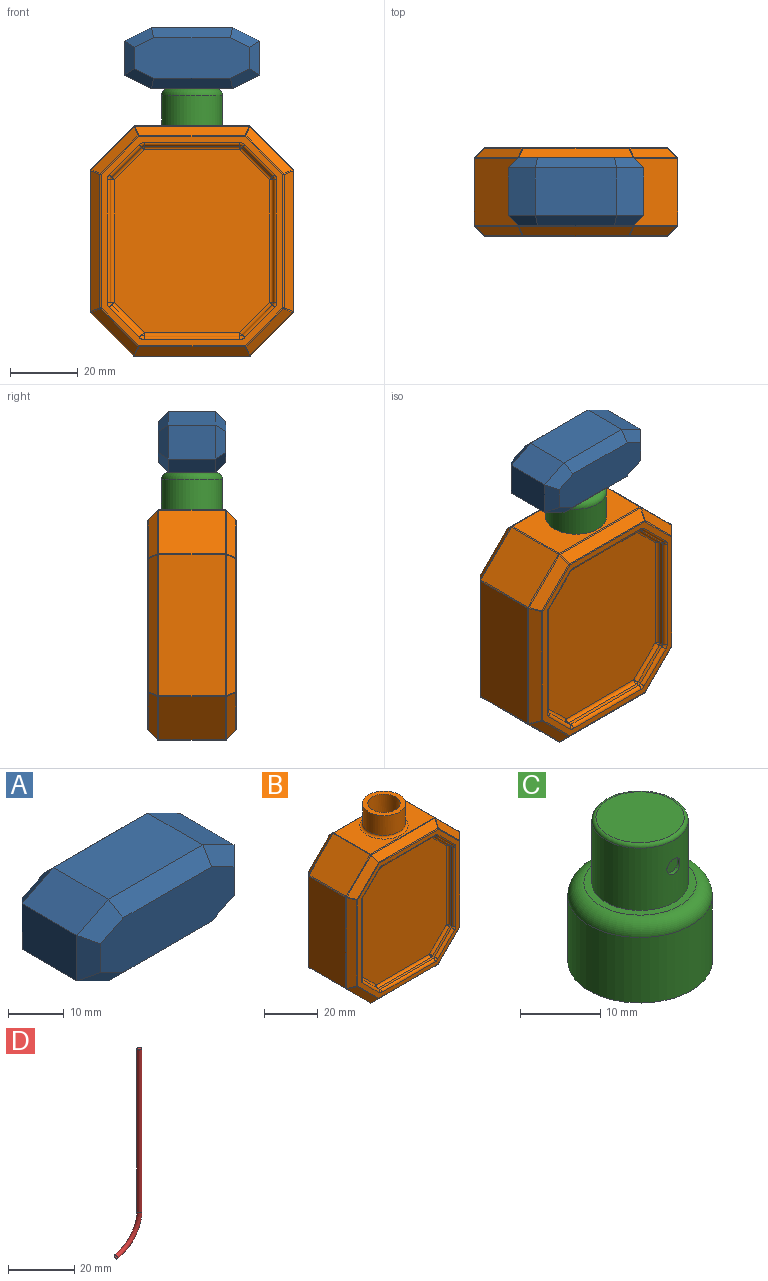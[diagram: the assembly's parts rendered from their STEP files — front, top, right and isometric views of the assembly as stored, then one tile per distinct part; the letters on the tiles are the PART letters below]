
ASSEMBLY  parts=4 mates=6
PART A: 29 faces, bbox 40x20x18 mm
  f0: plane 24x14mm, normal (0,0,1), area 336mm2, adj f1,f7,f16,f24
  f1: plane 14x8mm, normal (-0.45,0,0.89), area 125.2mm2, adj f0,f2,f14,f22
  f2: plane 14x10mm, normal (-1,0,0), area 140mm2, adj f1,f3,f12,f20
  f3: plane 14x8mm, normal (-0.45,0,-0.89), area 125.2mm2, adj f2,f4,f10,f18
  f4: plane 24x14mm, normal (0,0,-1), area 222.9mm2, adj f3,f5,f11,f19,f26
  f5: plane 14x8mm, normal (0.45,0,-0.89), area 125.2mm2, adj f4,f6,f13,f21
  f6: plane 14x10mm, normal (1,0,0), area 140mm2, adj f5,f7,f15,f23
  f7: plane 14x8mm, normal (0.45,0,0.89), area 125.2mm2, adj f0,f6,f17,f25
  f8: plane 34x12mm, normal (0,-1,0), area 375.4mm2, adj f18,f19,f20,f21,f22,f23,f24,f25
  f9: plane 34x12mm, normal (0,1,0), area 375.4mm2, adj f10,f11,f12,f13,f14,f15,f16,f17
  f10: plane 8.71x5.85mm, normal (-0.32,0.71,-0.63), area 32.5mm2, adj f3,f9,f11,f12
  f11: plane 24x3mm, normal (0,0.71,-0.71), area 98.8mm2, adj f4,f9,f10,f13
  f12: plane 10x3mm, normal (-0.71,0.71,0), area 34.6mm2, adj f2,f9,f10,f14
  f13: plane 8.71x5.85mm, normal (0.32,0.71,-0.63), area 32.5mm2, adj f5,f9,f11,f15
  f14: plane 8.71x5.85mm, normal (-0.32,0.71,0.63), area 32.5mm2, adj f1,f9,f12,f16
  f15: plane 10x3mm, normal (0.71,0.71,0), area 34.6mm2, adj f6,f9,f13,f17
  f16: plane 24x3mm, normal (0,0.71,0.71), area 98.8mm2, adj f0,f9,f14,f17
  f17: plane 8.71x5.85mm, normal (0.32,0.71,0.63), area 32.5mm2, adj f7,f9,f15,f16
  f18: plane 8.71x5.85mm, normal (-0.32,-0.71,-0.63), area 32.5mm2, adj f3,f8,f19,f20
  f19: plane 24x3mm, normal (0,-0.71,-0.71), area 98.8mm2, adj f4,f8,f18,f21
  f20: plane 10x3mm, normal (-0.71,-0.71,0), area 34.6mm2, adj f2,f8,f18,f22
  f21: plane 8.71x5.85mm, normal (0.32,-0.71,-0.63), area 32.5mm2, adj f5,f8,f19,f23
  f22: plane 8.71x5.85mm, normal (-0.32,-0.71,0.63), area 32.5mm2, adj f1,f8,f20,f24
  f23: plane 10x3mm, normal (0.71,-0.71,0), area 34.6mm2, adj f6,f8,f21,f25
  f24: plane 24x3mm, normal (0,-0.71,0.71), area 98.8mm2, adj f0,f8,f22,f25
  f25: plane 8.71x5.85mm, normal (0.32,-0.71,0.63), area 32.5mm2, adj f7,f8,f23,f24
  f26: cylinder r=6mm len=12mm, axis (0,0,-1), area 358.1mm2, adj f4,f28
  f27: plane 11x11mm, normal (0,0,-1), area 95mm2, adj f28
  f28: torus R=5.5mm, axis (0,0,-1), area 28.7mm2, adj f26,f27
PART B: 277 faces, bbox 60x26x78 mm
  f0: plane 19.59x12.71mm, normal (0.71,0,0.71), area 352mm2, adj f174,f175,f192,f193
  f1: plane 33.59x19.59mm, normal (0,0,1), area 403.3mm2, adj f185,f192,f199,f200,f214
  f2: plane 19.59x12.71mm, normal (-0.71,0,0.71), area 352mm2, adj f182,f183,f198,f199
  f3: plane 41.59x19.59mm, normal (-1,0,0), area 814.5mm2, adj f160,f161,f181,f182
  f4: plane 19.59x12.71mm, normal (-0.71,0,-0.71), area 352mm2, adj f141,f142,f159,f160
  f5: plane 33.59x19.59mm, normal (0,0,-1), area 657.8mm2, adj f129,f139,f140,f141
  f6: plane 19.59x12.71mm, normal (0.71,0,-0.71), area 352mm2, adj f138,f139,f154,f155
  f7: plane 41.59x19.59mm, normal (1,0,0), area 814.5mm2, adj f153,f154,f175,f176
  f8: plane 61.59x53.59mm, normal (0,-1,0), area 356.3mm2, adj f86,f90,f91,f95,f96,f100,f101,f105
  f9: plane 61.59x53.59mm, normal (0,1,0), area 356.3mm2, adj f46,f50,f51,f55,f56,f60,f61,f65
  f10: plane 13.83x13.83mm, normal (-0.5,0.71,-0.5), area 64.5mm2, adj f130,f131,f142,f143
  f11: plane 33.59x2.71mm, normal (0,0.71,-0.71), area 124.3mm2, adj f124,f128,f129,f130
  f12: plane 41.59x2.71mm, normal (-0.71,0.71,0), area 154.9mm2, adj f143,f144,f161,f162
  f13: plane 13.83x13.83mm, normal (0.5,0.71,-0.5), area 64.5mm2, adj f127,f128,f137,f138
  f14: plane 13.83x13.83mm, normal (-0.5,0.71,0.5), area 64.5mm2, adj f162,f163,f183,f184
  f15: plane 41.59x2.71mm, normal (0.71,0.71,0), area 154.9mm2, adj f136,f137,f152,f153
  f16: plane 33.59x2.71mm, normal (0,0.71,0.71), area 124.3mm2, adj f164,f173,f184,f185
  f17: plane 13.83x13.83mm, normal (0.5,0.71,0.5), area 64.5mm2, adj f151,f152,f173,f174
  f18: plane 13.83x13.83mm, normal (-0.5,-0.71,-0.5), area 64.5mm2, adj f158,f159,f179,f180
  f19: plane 33.59x2.71mm, normal (0,-0.71,-0.71), area 124.3mm2, adj f140,f156,f157,f158
  f20: plane 41.59x2.71mm, normal (-0.71,-0.71,0), area 154.9mm2, adj f180,f181,f196,f197
  f21: plane 13.83x13.83mm, normal (0.5,-0.71,-0.5), area 64.5mm2, adj f155,f156,f177,f178
  f22: plane 13.83x13.83mm, normal (-0.5,-0.71,0.5), area 64.5mm2, adj f197,f198,f207,f208
  f23: plane 41.59x2.71mm, normal (0.71,-0.71,0), area 154.9mm2, adj f176,f177,f194,f195
  f24: plane 33.59x2.71mm, normal (0,-0.71,0.71), area 124.3mm2, adj f200,f205,f208,f211
  f25: plane 13.83x13.83mm, normal (0.5,-0.71,0.5), area 64.5mm2, adj f193,f194,f205,f206
  f26: plane 36.2x1mm, normal (1,0,0), area 36.2mm2, adj f112,f117,f120,f123
  f27: plane 8.9x8.9mm, normal (0.71,0,0.71), area 12.6mm2, adj f109,f118,f119,f123
  f28: plane 28.2x1mm, normal (0,0,1), area 28.2mm2, adj f99,f108,f109,f110
  f29: plane 8.9x8.9mm, normal (-0.71,0,0.71), area 12.6mm2, adj f89,f98,f99,f100
  f30: plane 36.2x1mm, normal (-1,0,0), area 36.2mm2, adj f84,f88,f89,f90
  f31: plane 8.9x8.9mm, normal (-0.71,0,-0.71), area 12.6mm2, adj f84,f87,f91,f92
  f32: plane 28.2x1mm, normal (0,0,-1), area 28.2mm2, adj f92,f97,f101,f102
  f33: plane 8.9x8.9mm, normal (0.71,0,-0.71), area 12.6mm2, adj f102,f107,f111,f112
  f34: plane 54x46mm, normal (0,-1,0), area 2325.6mm2, adj f87,f88,f97,f98,f107,f108,f117,f118
  f35: plane 36.2x1mm, normal (-1,0,0), area 36.2mm2, adj f72,f77,f80,f83
  f36: plane 8.9x8.9mm, normal (-0.71,0,0.71), area 12.6mm2, adj f69,f78,f79,f83
  f37: plane 28.2x1mm, normal (0,0,1), area 28.2mm2, adj f59,f68,f69,f70
  f38: plane 8.9x8.9mm, normal (0.71,0,0.71), area 12.6mm2, adj f49,f58,f59,f60
  f39: plane 36.2x1mm, normal (1,0,0), area 36.2mm2, adj f44,f48,f49,f50
  f40: plane 8.9x8.9mm, normal (0.71,0,-0.71), area 12.6mm2, adj f44,f47,f51,f52
  f41: plane 28.2x1mm, normal (0,0,-1), area 28.2mm2, adj f52,f57,f61,f62
  f42: plane 8.9x8.9mm, normal (-0.71,0,-0.71), area 12.6mm2, adj f62,f67,f71,f72
  f43: plane 54x46mm, normal (0,1,0), area 2325.6mm2, adj f47,f48,f57,f58,f67,f68,f77,f78
  f44: cylinder r=1mm len=1mm, axis (0,-1,0), area 0.8mm2, adj f39,f40,f45,f46
  f45: sphere r=1mm, area 0.8mm2, adj f44,f47,f48
  f46: torus R=2mm, axis (0,-1,0), area 1.7mm2, adj f9,f44,f50,f51
  f47: cylinder r=1mm len=9.61mm, axis (0.71,0,0.71), area 19.8mm2, adj f40,f43,f45,f53
  f48: cylinder r=1mm len=36.2mm, axis (0,0,1), area 56.9mm2, adj f39,f43,f45,f54
  f49: cylinder r=1mm len=1mm, axis (0,-1,0), area 0.8mm2, adj f38,f39,f54,f55
  f50: cylinder r=1mm len=36.2mm, axis (0,0,1), area 56.9mm2, adj f9,f39,f46,f55
  f51: cylinder r=1mm len=9.61mm, axis (0.71,0,0.71), area 19.8mm2, adj f9,f40,f46,f56
  f52: cylinder r=1mm len=1mm, axis (0,-1,0), area 0.8mm2, adj f40,f41,f53,f56
  f53: sphere r=1mm, area 0.8mm2, adj f47,f52,f57
  f54: sphere r=1mm, area 0.8mm2, adj f48,f49,f58
  f55: torus R=2mm, axis (0,-1,0), area 1.7mm2, adj f9,f49,f50,f60
  f56: torus R=2mm, axis (0,-1,0), area 1.7mm2, adj f9,f51,f52,f61
  f57: cylinder r=1mm len=28.2mm, axis (1,0,0), area 44.3mm2, adj f41,f43,f53,f63
  f58: cylinder r=1mm len=9.61mm, axis (-0.71,0,0.71), area 19.8mm2, adj f38,f43,f54,f64
  f59: cylinder r=1mm len=1mm, axis (0,-1,0), area 0.8mm2, adj f37,f38,f64,f65
  f60: cylinder r=1mm len=9.61mm, axis (-0.71,0,0.71), area 19.8mm2, adj f9,f38,f55,f65
  f61: cylinder r=1mm len=28.2mm, axis (1,0,0), area 44.3mm2, adj f9,f41,f56,f66
  f62: cylinder r=1mm len=1mm, axis (0,-1,0), area 0.8mm2, adj f41,f42,f63,f66
  f63: sphere r=1mm, area 0.8mm2, adj f57,f62,f67
  f64: sphere r=1mm, area 0.8mm2, adj f58,f59,f68
  f65: torus R=2mm, axis (0,-1,0), area 1.7mm2, adj f9,f59,f60,f70
  f66: torus R=2mm, axis (0,-1,0), area 1.7mm2, adj f9,f61,f62,f71
  f67: cylinder r=1mm len=9.61mm, axis (0.71,0,-0.71), area 19.8mm2, adj f42,f43,f63,f73
  f68: cylinder r=1mm len=28.2mm, axis (-1,0,0), area 44.3mm2, adj f37,f43,f64,f74
  f69: cylinder r=1mm len=1mm, axis (0,-1,0), area 0.8mm2, adj f36,f37,f74,f75
  f70: cylinder r=1mm len=28.2mm, axis (-1,0,0), area 44.3mm2, adj f9,f37,f65,f75
  f71: cylinder r=1mm len=9.61mm, axis (0.71,0,-0.71), area 19.8mm2, adj f9,f42,f66,f76
  f72: cylinder r=1mm len=1mm, axis (0,-1,0), area 0.8mm2, adj f35,f42,f73,f76
  f73: sphere r=1mm, area 0.8mm2, adj f67,f72,f77
  f74: sphere r=1mm, area 0.8mm2, adj f68,f69,f78
  f75: torus R=2mm, axis (0,-1,0), area 1.7mm2, adj f9,f69,f70,f79
  f76: torus R=2mm, axis (0,-1,0), area 1.7mm2, adj f9,f71,f72,f80
  f77: cylinder r=1mm len=36.2mm, axis (0,0,-1), area 56.9mm2, adj f35,f43,f73,f81
  f78: cylinder r=1mm len=9.61mm, axis (-0.71,0,-0.71), area 19.8mm2, adj f36,f43,f74,f81
  f79: cylinder r=1mm len=9.61mm, axis (-0.71,0,-0.71), area 19.8mm2, adj f9,f36,f75,f82
  f80: cylinder r=1mm len=36.2mm, axis (0,0,-1), area 56.9mm2, adj f9,f35,f76,f82
  f81: sphere r=1mm, area 0.8mm2, adj f77,f78,f83
  f82: torus R=2mm, axis (0,-1,0), area 1.7mm2, adj f9,f79,f80,f83
  f83: cylinder r=1mm len=1mm, axis (0,-1,0), area 0.8mm2, adj f35,f36,f81,f82
  f84: cylinder r=1mm len=1mm, axis (0,1,0), area 0.8mm2, adj f30,f31,f85,f86
  f85: sphere r=1mm, area 0.8mm2, adj f84,f87,f88
  f86: torus R=2mm, axis (0,-1,0), area 1.7mm2, adj f8,f84,f90,f91
  f87: cylinder r=1mm len=9.61mm, axis (-0.71,0,0.71), area 19.8mm2, adj f31,f34,f85,f93
  f88: cylinder r=1mm len=36.2mm, axis (0,0,1), area 56.9mm2, adj f30,f34,f85,f94
  f89: cylinder r=1mm len=1mm, axis (0,1,0), area 0.8mm2, adj f29,f30,f94,f95
  f90: cylinder r=1mm len=36.2mm, axis (0,0,-1), area 56.9mm2, adj f8,f30,f86,f95
  f91: cylinder r=1mm len=9.61mm, axis (0.71,0,-0.71), area 19.8mm2, adj f8,f31,f86,f96
  f92: cylinder r=1mm len=1mm, axis (0,1,0), area 0.8mm2, adj f31,f32,f93,f96
  f93: sphere r=1mm, area 0.8mm2, adj f87,f92,f97
  f94: sphere r=1mm, area 0.8mm2, adj f88,f89,f98
  f95: torus R=2mm, axis (0,-1,0), area 1.7mm2, adj f8,f89,f90,f100
  f96: torus R=2mm, axis (0,-1,0), area 1.7mm2, adj f8,f91,f92,f101
  f97: cylinder r=1mm len=28.2mm, axis (-1,0,0), area 44.3mm2, adj f32,f34,f93,f103
  f98: cylinder r=1mm len=9.61mm, axis (0.71,0,0.71), area 19.8mm2, adj f29,f34,f94,f104
  f99: cylinder r=1mm len=1mm, axis (0,1,0), area 0.8mm2, adj f28,f29,f104,f105
  f100: cylinder r=1mm len=9.61mm, axis (-0.71,0,-0.71), area 19.8mm2, adj f8,f29,f95,f105
  f101: cylinder r=1mm len=28.2mm, axis (1,0,0), area 44.3mm2, adj f8,f32,f96,f106
  f102: cylinder r=1mm len=1mm, axis (0,1,0), area 0.8mm2, adj f32,f33,f103,f106
  f103: sphere r=1mm, area 0.8mm2, adj f97,f102,f107
  f104: sphere r=1mm, area 0.8mm2, adj f98,f99,f108
  f105: torus R=2mm, axis (0,-1,0), area 1.7mm2, adj f8,f99,f100,f110
  f106: torus R=2mm, axis (0,-1,0), area 1.7mm2, adj f8,f101,f102,f111
  f107: cylinder r=1mm len=9.61mm, axis (-0.71,0,-0.71), area 19.8mm2, adj f33,f34,f103,f113
  f108: cylinder r=1mm len=28.2mm, axis (1,0,0), area 44.3mm2, adj f28,f34,f104,f114
  f109: cylinder r=1mm len=1mm, axis (0,1,0), area 0.8mm2, adj f27,f28,f114,f115
  f110: cylinder r=1mm len=28.2mm, axis (-1,0,0), area 44.3mm2, adj f8,f28,f105,f115
  f111: cylinder r=1mm len=9.61mm, axis (0.71,0,0.71), area 19.8mm2, adj f8,f33,f106,f116
  f112: cylinder r=1mm len=1mm, axis (0,1,0), area 0.8mm2, adj f26,f33,f113,f116
  f113: sphere r=1mm, area 0.8mm2, adj f107,f112,f117
  f114: sphere r=1mm, area 0.8mm2, adj f108,f109,f118
  f115: torus R=2mm, axis (0,-1,0), area 1.7mm2, adj f8,f109,f110,f119
  f116: torus R=2mm, axis (0,-1,0), area 1.7mm2, adj f8,f111,f112,f120
  f117: cylinder r=1mm len=36.2mm, axis (0,0,-1), area 56.9mm2, adj f26,f34,f113,f121
  f118: cylinder r=1mm len=9.61mm, axis (0.71,0,-0.71), area 19.8mm2, adj f27,f34,f114,f121
  f119: cylinder r=1mm len=9.61mm, axis (-0.71,0,0.71), area 19.8mm2, adj f8,f27,f115,f122
  f120: cylinder r=1mm len=36.2mm, axis (0,0,1), area 56.9mm2, adj f8,f26,f116,f122
  f121: sphere r=1mm, area 0.8mm2, adj f117,f118,f123
  f122: torus R=2mm, axis (0,-1,0), area 1.7mm2, adj f8,f119,f120,f123
  f123: cylinder r=1mm len=1mm, axis (0,1,0), area 0.8mm2, adj f26,f27,f121,f122
  f124: cylinder r=0.5mm len=31.34mm, axis (1,0,0), area 12.3mm2, adj f9,f11,f125,f126
  f125: sphere r=0.5mm, area 0.1mm2, adj f124,f127,f128
  f126: sphere r=0.5mm, area 0.1mm2, adj f124,f130,f131
  f127: cylinder r=0.5mm len=11.37mm, axis (0.71,0,0.71), area 6.2mm2, adj f9,f13,f125,f132
  f128: cylinder r=0.5mm len=2.81mm, axis (-0.28,0.68,0.68), area 1.1mm2, adj f11,f13,f125,f133
  f129: cylinder r=0.5mm len=33.59mm, axis (1,0,0), area 13.2mm2, adj f5,f11,f133,f134
  f130: cylinder r=0.5mm len=2.81mm, axis (-0.28,-0.68,-0.68), area 1.1mm2, adj f10,f11,f126,f134
  f131: cylinder r=0.5mm len=11.37mm, axis (-0.71,0,0.71), area 6.2mm2, adj f9,f10,f126,f135
  f132: sphere r=0.5mm, area 0.1mm2, adj f127,f136,f137
  f133: sphere r=0.5mm, area 0.1mm2, adj f128,f129,f138,f139
  f134: sphere r=0.5mm, area 0.1mm2, adj f129,f130,f141,f142
  f135: sphere r=0.5mm, area 0.1mm2, adj f131,f143,f144
  f136: cylinder r=0.5mm len=39.34mm, axis (0,0,-1), area 15.5mm2, adj f9,f15,f132,f145
  f137: cylinder r=0.5mm len=2.81mm, axis (0.68,-0.68,-0.28), area 1.1mm2, adj f13,f15,f132,f146
  f138: cylinder r=0.5mm len=12.81mm, axis (0.71,0,0.71), area 7.1mm2, adj f6,f13,f133,f146
  f139: cylinder r=0.5mm len=19.59mm, axis (0,1,0), area 7.7mm2, adj f5,f6,f133,f147
  f140: cylinder r=0.5mm len=33.59mm, axis (1,0,0), area 13.2mm2, adj f5,f19,f147,f148
  f141: cylinder r=0.5mm len=19.59mm, axis (0,-1,0), area 7.7mm2, adj f4,f5,f134,f148
  f142: cylinder r=0.5mm len=12.81mm, axis (0.71,0,-0.71), area 7.1mm2, adj f4,f10,f134,f149
  f143: cylinder r=0.5mm len=2.81mm, axis (0.68,0.68,0.28), area 1.1mm2, adj f10,f12,f135,f149
  f144: cylinder r=0.5mm len=39.34mm, axis (0,0,-1), area 15.5mm2, adj f9,f12,f135,f150
  f145: sphere r=0.5mm, area 0.1mm2, adj f136,f151,f152
  f146: sphere r=0.5mm, area 0.1mm2, adj f137,f138,f153,f154
  f147: sphere r=0.5mm, area 0.1mm2, adj f139,f140,f155,f156
  f148: sphere r=0.5mm, area 0.1mm2, adj f140,f141,f158,f159
  f149: sphere r=0.5mm, area 0.1mm2, adj f142,f143,f160,f161
  f150: sphere r=0.5mm, area 0.1mm2, adj f144,f162,f163
  f151: cylinder r=0.5mm len=11.37mm, axis (0.71,0,-0.71), area 6.2mm2, adj f9,f17,f145,f165
  f152: cylinder r=0.5mm len=2.81mm, axis (-0.68,0.68,-0.28), area 1.1mm2, adj f15,f17,f145,f166
  f153: cylinder r=0.5mm len=41.59mm, axis (0,0,1), area 16.3mm2, adj f7,f15,f146,f166
  f154: cylinder r=0.5mm len=19.59mm, axis (0,-1,0), area 7.7mm2, adj f6,f7,f146,f167
  f155: cylinder r=0.5mm len=12.81mm, axis (0.71,0,0.71), area 7.1mm2, adj f6,f21,f147,f167
  f156: cylinder r=0.5mm len=2.81mm, axis (0.28,0.68,-0.68), area 1.1mm2, adj f19,f21,f147,f168
  f157: cylinder r=0.5mm len=31.34mm, axis (-1,0,0), area 12.3mm2, adj f8,f19,f168,f169
  f158: cylinder r=0.5mm len=2.81mm, axis (0.28,-0.68,0.68), area 1.1mm2, adj f18,f19,f148,f169
  f159: cylinder r=0.5mm len=12.81mm, axis (0.71,0,-0.71), area 7.1mm2, adj f4,f18,f148,f170
  f160: cylinder r=0.5mm len=19.59mm, axis (0,-1,0), area 7.7mm2, adj f3,f4,f149,f170
  f161: cylinder r=0.5mm len=41.59mm, axis (0,0,-1), area 16.3mm2, adj f3,f12,f149,f171
  f162: cylinder r=0.5mm len=2.81mm, axis (0.68,0.68,-0.28), area 1.1mm2, adj f12,f14,f150,f171
  f163: cylinder r=0.5mm len=11.37mm, axis (0.71,0,0.71), area 6.2mm2, adj f9,f14,f150,f172
  f164: cylinder r=0.5mm len=31.34mm, axis (1,0,0), area 12.3mm2, adj f9,f16,f165,f172
  f165: sphere r=0.5mm, area 0.1mm2, adj f151,f164,f173
  f166: sphere r=0.5mm, area 0.1mm2, adj f152,f153,f174,f175
  f167: sphere r=0.5mm, area 0.1mm2, adj f154,f155,f176,f177
  f168: sphere r=0.5mm, area 0.1mm2, adj f156,f157,f178
  f169: sphere r=0.5mm, area 0.1mm2, adj f157,f158,f179
  f170: sphere r=0.5mm, area 0.1mm2, adj f159,f160,f180,f181
  f171: sphere r=0.5mm, area 0.1mm2, adj f161,f162,f182,f183
  f172: sphere r=0.5mm, area 0.1mm2, adj f163,f164,f184
  f173: cylinder r=0.5mm len=2.81mm, axis (0.28,-0.68,0.68), area 1.1mm2, adj f16,f17,f165,f186
  f174: cylinder r=0.5mm len=12.81mm, axis (-0.71,0,0.71), area 7.1mm2, adj f0,f17,f166,f186
  f175: cylinder r=0.5mm len=19.59mm, axis (0,1,0), area 7.7mm2, adj f0,f7,f166,f187
  f176: cylinder r=0.5mm len=41.59mm, axis (0,0,1), area 16.3mm2, adj f7,f23,f167,f187
  f177: cylinder r=0.5mm len=2.81mm, axis (-0.68,-0.68,0.28), area 1.1mm2, adj f21,f23,f167,f188
  f178: cylinder r=0.5mm len=11.37mm, axis (-0.71,0,-0.71), area 6.2mm2, adj f8,f21,f168,f188
  f179: cylinder r=0.5mm len=11.37mm, axis (0.71,0,-0.71), area 6.2mm2, adj f8,f18,f169,f189
  f180: cylinder r=0.5mm len=2.81mm, axis (-0.68,0.68,-0.28), area 1.1mm2, adj f18,f20,f170,f189
  f181: cylinder r=0.5mm len=41.59mm, axis (0,0,-1), area 16.3mm2, adj f3,f20,f170,f190
  f182: cylinder r=0.5mm len=19.59mm, axis (0,-1,0), area 7.7mm2, adj f2,f3,f171,f190
  f183: cylinder r=0.5mm len=12.81mm, axis (-0.71,0,-0.71), area 7.1mm2, adj f2,f14,f171,f191
  f184: cylinder r=0.5mm len=2.81mm, axis (-0.28,-0.68,0.68), area 1.1mm2, adj f14,f16,f172,f191
  f185: cylinder r=0.5mm len=33.59mm, axis (-1,0,0), area 13.2mm2, adj f1,f16,f186,f191
  f186: sphere r=0.5mm, area 0.1mm2, adj f173,f174,f185,f192
  f187: sphere r=0.5mm, area 0.1mm2, adj f175,f176,f193,f194
  f188: sphere r=0.5mm, area 0.1mm2, adj f177,f178,f195
  f189: sphere r=0.5mm, area 0.1mm2, adj f179,f180,f196
  f190: sphere r=0.5mm, area 0.1mm2, adj f181,f182,f197,f198
  f191: sphere r=0.5mm, area 0.1mm2, adj f183,f184,f185,f199
  f192: cylinder r=0.5mm len=19.59mm, axis (0,1,0), area 7.7mm2, adj f0,f1,f186,f201
  f193: cylinder r=0.5mm len=12.81mm, axis (-0.71,0,0.71), area 7.1mm2, adj f0,f25,f187,f201
  f194: cylinder r=0.5mm len=2.81mm, axis (0.68,0.68,0.28), area 1.1mm2, adj f23,f25,f187,f202
  f195: cylinder r=0.5mm len=39.34mm, axis (0,0,1), area 15.5mm2, adj f8,f23,f188,f202
  f196: cylinder r=0.5mm len=39.34mm, axis (0,0,1), area 15.5mm2, adj f8,f20,f189,f203
  f197: cylinder r=0.5mm len=2.81mm, axis (-0.68,0.68,0.28), area 1.1mm2, adj f20,f22,f190,f203
  f198: cylinder r=0.5mm len=12.81mm, axis (-0.71,0,-0.71), area 7.1mm2, adj f2,f22,f190,f204
  f199: cylinder r=0.5mm len=19.59mm, axis (0,1,0), area 7.7mm2, adj f1,f2,f191,f204
  f200: cylinder r=0.5mm len=33.59mm, axis (-1,0,0), area 13.2mm2, adj f1,f24,f201,f204
  f201: sphere r=0.5mm, area 0.1mm2, adj f192,f193,f200,f205
  f202: sphere r=0.5mm, area 0.1mm2, adj f194,f195,f206
  f203: sphere r=0.5mm, area 0.1mm2, adj f196,f197,f207
  f204: sphere r=0.5mm, area 0.1mm2, adj f198,f199,f200,f208
  f205: cylinder r=0.5mm len=2.81mm, axis (-0.28,-0.68,-0.68), area 1.1mm2, adj f24,f25,f201,f209
  f206: cylinder r=0.5mm len=11.37mm, axis (-0.71,0,0.71), area 6.2mm2, adj f8,f25,f202,f209
  f207: cylinder r=0.5mm len=11.37mm, axis (-0.71,0,-0.71), area 6.2mm2, adj f8,f22,f203,f210
  f208: cylinder r=0.5mm len=2.81mm, axis (0.28,-0.68,-0.68), area 1.1mm2, adj f22,f24,f204,f210
  f209: sphere r=0.5mm, area 0.1mm2, adj f205,f206,f211
  f210: sphere r=0.5mm, area 0.1mm2, adj f207,f208,f211
  f211: cylinder r=0.5mm len=31.34mm, axis (-1,0,0), area 12.3mm2, adj f8,f24,f209,f210
  f212: cylinder r=8mm len=16mm, axis (0,0,-1), area 452.4mm2, adj f213,f214
  f213: plane 16x16mm, normal (0,0,1), area 88mm2, adj f212,f275
  f214: torus R=9mm, axis (0,0,-1), area 82.5mm2, adj f1,f212
  f215: plane 18.34x11.83mm, normal (-0.71,0,-0.71), area 306.8mm2, adj f216,f222,f232,f240
  f216: plane 32.34x18.34mm, normal (0,0,-1), area 338.8mm2, adj f215,f217,f231,f239,f276
  f217: plane 18.34x11.83mm, normal (0.71,0,-0.71), area 306.8mm2, adj f216,f218,f229,f237
  f218: plane 40.34x18.34mm, normal (1,0,0), area 740mm2, adj f217,f219,f227,f235
  f219: plane 18.34x11.83mm, normal (0.71,0,0.71), area 306.8mm2, adj f218,f220,f225,f233
  f220: plane 32.34x18.34mm, normal (0,0,1), area 593.3mm2, adj f219,f221,f226,f234
  f221: plane 18.34x11.83mm, normal (-0.71,0,0.71), area 306.8mm2, adj f220,f222,f228,f236
  f222: plane 40.34x18.34mm, normal (-1,0,0), area 740mm2, adj f215,f221,f230,f238
  f223: plane 60.34x52.34mm, normal (0,1,0), area 35.8mm2, adj f233,f234,f235,f236,f237,f238,f239,f240
  f224: plane 60.34x52.34mm, normal (0,-1,0), area 35.8mm2, adj f225,f226,f227,f228,f229,f230,f231,f232
  f225: plane 12.59x12.59mm, normal (0.5,-0.71,0.5), area 41.3mm2, adj f219,f224,f226,f227
  f226: plane 32.34x1.83mm, normal (0,-0.71,0.71), area 81.7mm2, adj f220,f224,f225,f228
  f227: plane 40.34x1.83mm, normal (0.71,-0.71,0), area 102.4mm2, adj f218,f224,f225,f229
  f228: plane 12.59x12.59mm, normal (-0.5,-0.71,0.5), area 41.3mm2, adj f221,f224,f226,f230
  f229: plane 12.59x12.59mm, normal (0.5,-0.71,-0.5), area 41.3mm2, adj f217,f224,f227,f231
  f230: plane 40.34x1.83mm, normal (-0.71,-0.71,0), area 102.4mm2, adj f222,f224,f228,f232
  f231: plane 32.34x1.83mm, normal (0,-0.71,-0.71), area 81.7mm2, adj f216,f224,f229,f232
  f232: plane 12.59x12.59mm, normal (-0.5,-0.71,-0.5), area 41.3mm2, adj f215,f224,f230,f231
  f233: plane 12.59x12.59mm, normal (0.5,0.71,0.5), area 41.3mm2, adj f219,f223,f234,f235
  f234: plane 32.34x1.83mm, normal (0,0.71,0.71), area 81.7mm2, adj f220,f223,f233,f236
  f235: plane 40.34x1.83mm, normal (0.71,0.71,0), area 102.4mm2, adj f218,f223,f233,f237
  f236: plane 12.59x12.59mm, normal (-0.5,0.71,0.5), area 41.3mm2, adj f221,f223,f234,f238
  f237: plane 12.59x12.59mm, normal (0.5,0.71,-0.5), area 41.3mm2, adj f217,f223,f235,f239
  f238: plane 40.34x1.83mm, normal (-0.71,0.71,0), area 102.4mm2, adj f222,f223,f236,f240
  f239: plane 32.34x1.83mm, normal (0,0.71,-0.71), area 81.7mm2, adj f216,f223,f237,f240
  f240: plane 12.59x12.59mm, normal (-0.5,0.71,-0.5), area 41.3mm2, adj f215,f223,f238,f239
  f241: plane 54x46mm, normal (0,1,0), area 2325.6mm2, adj f260,f261,f264,f265,f268,f269,f272,f273
  f242: plane 54x46mm, normal (0,-1,0), area 2325.6mm2, adj f244,f245,f248,f249,f252,f253,f256,f257
  f243: sphere r=3mm, area 7.1mm2, adj f224,f244,f245
  f244: cylinder r=3mm len=11.02mm, axis (0.71,0,0.71), area 59.3mm2, adj f224,f242,f243,f246
  f245: cylinder r=3mm len=36.2mm, axis (0,0,1), area 170.6mm2, adj f224,f242,f243,f247
  f246: sphere r=3mm, area 7.1mm2, adj f224,f244,f248
  f247: sphere r=3mm, area 7.1mm2, adj f224,f245,f249
  f248: cylinder r=3mm len=28.2mm, axis (1,0,0), area 132.9mm2, adj f224,f242,f246,f250
  f249: cylinder r=3mm len=11.02mm, axis (-0.71,0,0.71), area 59.3mm2, adj f224,f242,f247,f251
  f250: sphere r=3mm, area 7.1mm2, adj f224,f248,f252
  f251: sphere r=3mm, area 7.1mm2, adj f224,f249,f253
  f252: cylinder r=3mm len=11.02mm, axis (0.71,0,-0.71), area 59.3mm2, adj f224,f242,f250,f254
  f253: cylinder r=3mm len=28.2mm, axis (-1,0,0), area 132.9mm2, adj f224,f242,f251,f255
  f254: sphere r=3mm, area 7.1mm2, adj f224,f252,f256
  f255: sphere r=3mm, area 7.1mm2, adj f224,f253,f257
  f256: cylinder r=3mm len=36.2mm, axis (0,0,-1), area 170.6mm2, adj f224,f242,f254,f258
  f257: cylinder r=3mm len=11.02mm, axis (-0.71,0,-0.71), area 59.3mm2, adj f224,f242,f255,f258
  f258: sphere r=3mm, area 7.1mm2, adj f224,f256,f257
  f259: sphere r=3mm, area 7.1mm2, adj f223,f260,f261
  f260: cylinder r=3mm len=11.02mm, axis (-0.71,0,0.71), area 59.3mm2, adj f223,f241,f259,f262
  f261: cylinder r=3mm len=36.2mm, axis (0,0,1), area 170.6mm2, adj f223,f241,f259,f263
  f262: sphere r=3mm, area 7.1mm2, adj f223,f260,f264
  f263: sphere r=3mm, area 7.1mm2, adj f223,f261,f265
  f264: cylinder r=3mm len=28.2mm, axis (-1,0,0), area 132.9mm2, adj f223,f241,f262,f266
  f265: cylinder r=3mm len=11.02mm, axis (0.71,0,0.71), area 59.3mm2, adj f223,f241,f263,f267
  f266: sphere r=3mm, area 7.1mm2, adj f223,f264,f268
  f267: sphere r=3mm, area 7.1mm2, adj f223,f265,f269
  f268: cylinder r=3mm len=11.02mm, axis (-0.71,0,-0.71), area 59.3mm2, adj f223,f241,f266,f270
  f269: cylinder r=3mm len=28.2mm, axis (1,0,0), area 132.9mm2, adj f223,f241,f267,f271
  f270: sphere r=3mm, area 7.1mm2, adj f223,f268,f272
  f271: sphere r=3mm, area 7.1mm2, adj f223,f269,f273
  f272: cylinder r=3mm len=36.2mm, axis (0,0,-1), area 170.6mm2, adj f223,f241,f270,f274
  f273: cylinder r=3mm len=11.02mm, axis (0.71,0,-0.71), area 59.3mm2, adj f223,f241,f271,f274
  f274: sphere r=3mm, area 7.1mm2, adj f223,f272,f273
  f275: cylinder r=6mm len=12mm, axis (0,0,-1), area 339.3mm2, adj f213,f276
  f276: torus R=9mm, axis (0,0,-1), area 209.9mm2, adj f216,f275
PART C: 11 faces, bbox 19.5x19.5x22 mm
  f0: cylinder r=6mm len=12mm, axis (0,0,-1), area 354mm2, adj f2,f8,f9
  f1: cylinder r=9mm len=18mm, axis (0,0,-1), area 565.5mm2, adj f3,f6
  f2: plane 14x14mm, normal (0,0,1), area 40.8mm2, adj f0,f6
  f3: plane 18x18mm, normal (0,0,-1), area 53.4mm2, adj f1,f4
  f4: cylinder r=8mm len=16mm, axis (0,0,-1), area 552.9mm2, adj f3,f5
  f5: plane 16x16mm, normal (0,0,-1), area 201.1mm2, adj f4
  f6: torus R=7mm, axis (0,0,1), area 163.3mm2, adj f1,f2
  f7: plane 11x11mm, normal (0,0,1), area 95mm2, adj f8
  f8: torus R=5.5mm, axis (0,0,1), area 28.7mm2, adj f0,f7
  f9: cylinder r=1.15mm len=2.3mm, axis (0,1,0), area 3.2mm2, adj f0,f10
  f10: plane 2.3x2.3mm, normal (0,-1,0), area 4.2mm2, adj f9
PART D: 7 faces, bbox 11.9x1.5x73.6 mm
  f0: plane 1.5x1.5mm, normal (0,0,1), area 1.8mm2, adj f2
  f1: plane 1.5x1.48mm, normal (-0.99,0,-0.17), area 0.8mm2, adj f3,f6
  f2: cylinder r=0.75mm len=60mm, axis (0,0,-1), area 282.7mm2, adj f0,f3
  f3: torus R=12mm, axis (0,1,0), area 79.4mm2, adj f1,f2
  f4: plane 1.1x1.1mm, normal (0,0,-1), area 1mm2, adj f5
  f5: cylinder r=0.55mm len=59.8mm, axis (0,0,-1), area 206.7mm2, adj f4,f6
  f6: torus R=12mm, axis (0,1,0), area 58.2mm2, adj f1,f5
PLACE A t=(-20,10,79)mm
PLACE B t=(0,0,34)mm
PLACE C t=(0,0,67)mm
PLACE D t=(0,0,67)mm
MATE slider D.f2 <-> C.f0  axis (0,0,1) through (0,0,78)mm
MATE slider C.f0 <-> A.f26  axis (0,0,-1) through (0,0,83.75)mm
MATE slider B.f214 <-> C.f0  axis (0,0,-1) through (0,0,73.5)mm
MATE planar B.f212 <-> C.f0  axis (0,0,1) through (0,0,78)mm
MATE planar C.f0 <-> D.f2  axis (0,0,-1) through (0,0,78)mm
MATE planar A.f26 <-> C.f0  axis (0,0,-1) through (0,0,89)mm
